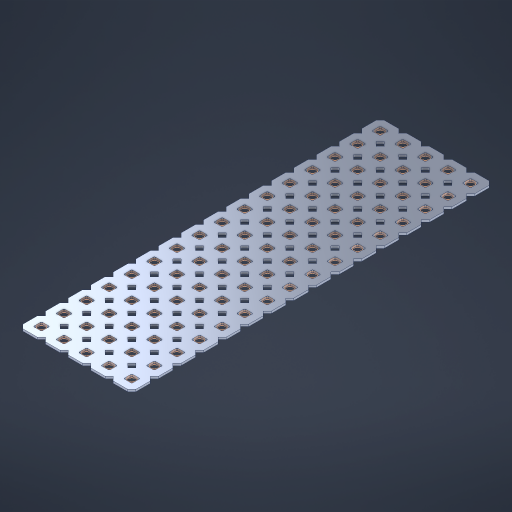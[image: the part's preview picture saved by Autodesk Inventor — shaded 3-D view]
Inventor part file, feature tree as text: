
AUTODESK INVENTOR PART (.ipt)
format: ipt  version: 2023 (Build 270158000, 158)  size: 1,189,376 bytes
history: native  units: in
note: dims shown in document units (in); Inventor stores cm internally (conversion verified against a paired STEP export)
features: other x81, extrude x79, sketch x2, pattern_linear x1
ambient origin geometry x8: Origin, YZ Plane, XZ Plane, XY Plane, X Axis, Y Axis, Z Axis, Center Point
bodies: Solid1 (feature_tree), Body (feature_tree)
feature tree (163):
  pattern_linear  "Rectangular Pattern1"  Spacing1=0.09in  [1 undecoded]
  sketch  "Sketch1"  dims[d1=0.5in]
  sketch  "Sketch2"  dims[d2=0.182in d3=0.09in d4=0.09in d5=0.09in d6=0.09in d7=0.09in d8=0.09in d9=0.09in d10=0.09in d11=0.02in d13=0.0in d14=0.172in d15=0.0625in d16=0.0in d19=0.5in d22=0.5in]
  other  "Srf1"
  other  "Srf126"
  other  "Srf127"
  other  "Srf128"
  other  "Srf129"
  other  "Srf130"
  other  "Srf131"
  other  "Srf250"
  other  "Srf251"
  other  "Srf252"
  other  "Srf253"
  other  "Srf254"
  other  "Srf255"
  other  "Srf256"
  other  "Srf257"
  other  "Srf258"
  other  "Srf268"
  other  "Srf269"
  other  "Srf270"
  other  "Srf271"
  other  "Srf272"
  other  "Srf273"
  other  "Srf274"
  other  "Srf275"
  other  "Srf276"
  other  "Srf277"
  other  "Srf278"
  other  "Srf279"
  other  "Srf280"
  other  "Srf281"
  other  "Srf282"
  other  "Srf283"
  other  "Srf293"
  other  "Srf294"
  other  "Srf295"
  other  "Srf296"
  other  "Srf297"
  other  "Srf298"
  other  "Srf299"
  other  "Srf300"
  other  "Srf301"
  other  "Srf302"
  other  "Srf303"
  other  "Srf304"
  other  "Srf305"
  other  "Srf306"
  other  "Srf307"
  other  "Srf308"
  other  "Srf318"
  other  "Srf319"
  other  "Srf320"
  other  "Srf321"
  other  "Srf322"
  other  "Srf323"
  other  "Srf324"
  other  "Srf325"
  other  "Srf326"
  other  "Srf327"
  other  "Srf328"
  other  "Srf329"
  other  "Srf330"
  other  "Srf331"
  other  "Srf332"
  other  "Srf333"
  other  "Srf343"
  other  "Srf344"
  other  "Srf345"
  other  "Srf346"
  other  "Srf347"
  other  "Srf348"
  other  "Srf349"
  other  "Srf350"
  other  "Srf351"
  other  "Srf352"
  other  "Srf353"
  other  "Srf354"
  other  "Srf355"
  other  "Srf356"
  other  "Srf357"
  other  "Srf358"
  other  "Circle"
  extrude  "ExtrusionSrf126"  Depth=0.09in
  extrude  "ExtrusionSrf127"  Depth=0.09in
  extrude  "ExtrusionSrf128"  Depth=0.09in
  extrude  "ExtrusionSrf129"  Depth=0.09in
  extrude  "ExtrusionSrf130"  Depth=0.09in
  extrude  "ExtrusionSrf131"  Depth=0.09in
  extrude  "ExtrusionSrf250"  Depth=0.09in
  extrude  "ExtrusionSrf251"  Depth=0.02in
  extrude  "ExtrusionSrf252"  TaperAngle=0.0deg  [1 undecoded]
  extrude  "ExtrusionSrf253"  Depth=0.5in
  extrude  "ExtrusionSrf254"  Depth=0.5in TaperAngle=0.0deg
  extrude  "ExtrusionSrf255"  Depth=0.5in
  extrude  "ExtrusionSrf256"  Depth=0.5in
  extrude  "ExtrusionSrf257"  [1 undecoded]
  extrude  "ExtrusionSrf258"  [1 undecoded]
  extrude  "ExtrusionSrf268"  [1 undecoded]
  extrude  "ExtrusionSrf269"  [1 undecoded]
  extrude  "ExtrusionSrf270"  [1 undecoded]
  extrude  "ExtrusionSrf271"  [1 undecoded]
  extrude  "ExtrusionSrf272"  [1 undecoded]
  extrude  "ExtrusionSrf273"  [1 undecoded]
  extrude  "ExtrusionSrf274"  [1 undecoded]
  extrude  "ExtrusionSrf275"  [1 undecoded]
  extrude  "ExtrusionSrf276"  [1 undecoded]
  extrude  "ExtrusionSrf277"  [1 undecoded]
  extrude  "ExtrusionSrf278"  [1 undecoded]
  extrude  "ExtrusionSrf279"  [1 undecoded]
  extrude  "ExtrusionSrf280"  [1 undecoded]
  extrude  "ExtrusionSrf281"  [1 undecoded]
  extrude  "ExtrusionSrf282"  [1 undecoded]
  extrude  "ExtrusionSrf283"  [1 undecoded]
  extrude  "ExtrusionSrf293"  [1 undecoded]
  extrude  "ExtrusionSrf294"  [1 undecoded]
  extrude  "ExtrusionSrf295"  [1 undecoded]
  extrude  "ExtrusionSrf296"  [1 undecoded]
  extrude  "ExtrusionSrf297"  [1 undecoded]
  extrude  "ExtrusionSrf298"  [1 undecoded]
  extrude  "ExtrusionSrf299"  [1 undecoded]
  extrude  "ExtrusionSrf300"  [1 undecoded]
  extrude  "ExtrusionSrf301"  [1 undecoded]
  extrude  "ExtrusionSrf302"  [1 undecoded]
  extrude  "ExtrusionSrf303"  [1 undecoded]
  extrude  "ExtrusionSrf304"  [1 undecoded]
  extrude  "ExtrusionSrf305"  [1 undecoded]
  extrude  "ExtrusionSrf306"  [1 undecoded]
  extrude  "ExtrusionSrf307"  [1 undecoded]
  extrude  "ExtrusionSrf308"  [1 undecoded]
  extrude  "ExtrusionSrf318"  [1 undecoded]
  extrude  "ExtrusionSrf319"  [1 undecoded]
  extrude  "ExtrusionSrf320"  [1 undecoded]
  extrude  "ExtrusionSrf321"  [1 undecoded]
  extrude  "ExtrusionSrf322"  [1 undecoded]
  extrude  "ExtrusionSrf323"  [1 undecoded]
  extrude  "ExtrusionSrf324"  [1 undecoded]
  extrude  "ExtrusionSrf325"  [1 undecoded]
  extrude  "ExtrusionSrf326"  [1 undecoded]
  extrude  "ExtrusionSrf327"  [1 undecoded]
  extrude  "ExtrusionSrf328"  [1 undecoded]
  extrude  "ExtrusionSrf329"  [1 undecoded]
  extrude  "ExtrusionSrf330"  [1 undecoded]
  extrude  "ExtrusionSrf331"  [1 undecoded]
  extrude  "ExtrusionSrf332"  [1 undecoded]
  extrude  "ExtrusionSrf333"  [1 undecoded]
  extrude  "ExtrusionSrf343"  [1 undecoded]
  extrude  "ExtrusionSrf344"  [1 undecoded]
  extrude  "ExtrusionSrf345"  [1 undecoded]
  extrude  "ExtrusionSrf346"  [1 undecoded]
  extrude  "ExtrusionSrf347"  [1 undecoded]
  extrude  "ExtrusionSrf348"  [1 undecoded]
  extrude  "ExtrusionSrf349"  [1 undecoded]
  extrude  "ExtrusionSrf350"  [1 undecoded]
  extrude  "ExtrusionSrf351"  [1 undecoded]
  extrude  "ExtrusionSrf352"  [1 undecoded]
  extrude  "ExtrusionSrf353"  [1 undecoded]
  extrude  "ExtrusionSrf354"  [1 undecoded]
  extrude  "ExtrusionSrf355"  [1 undecoded]
  extrude  "ExtrusionSrf356"  [1 undecoded]
  extrude  "ExtrusionSrf357"  [1 undecoded]
  extrude  "ExtrusionSrf358"  [1 undecoded]
note: 68 required parameter values undecoded (feature->parameter linkage not recoverable at this tier; creation-order binding heuristic only, values carry confidence <= 0.55)
